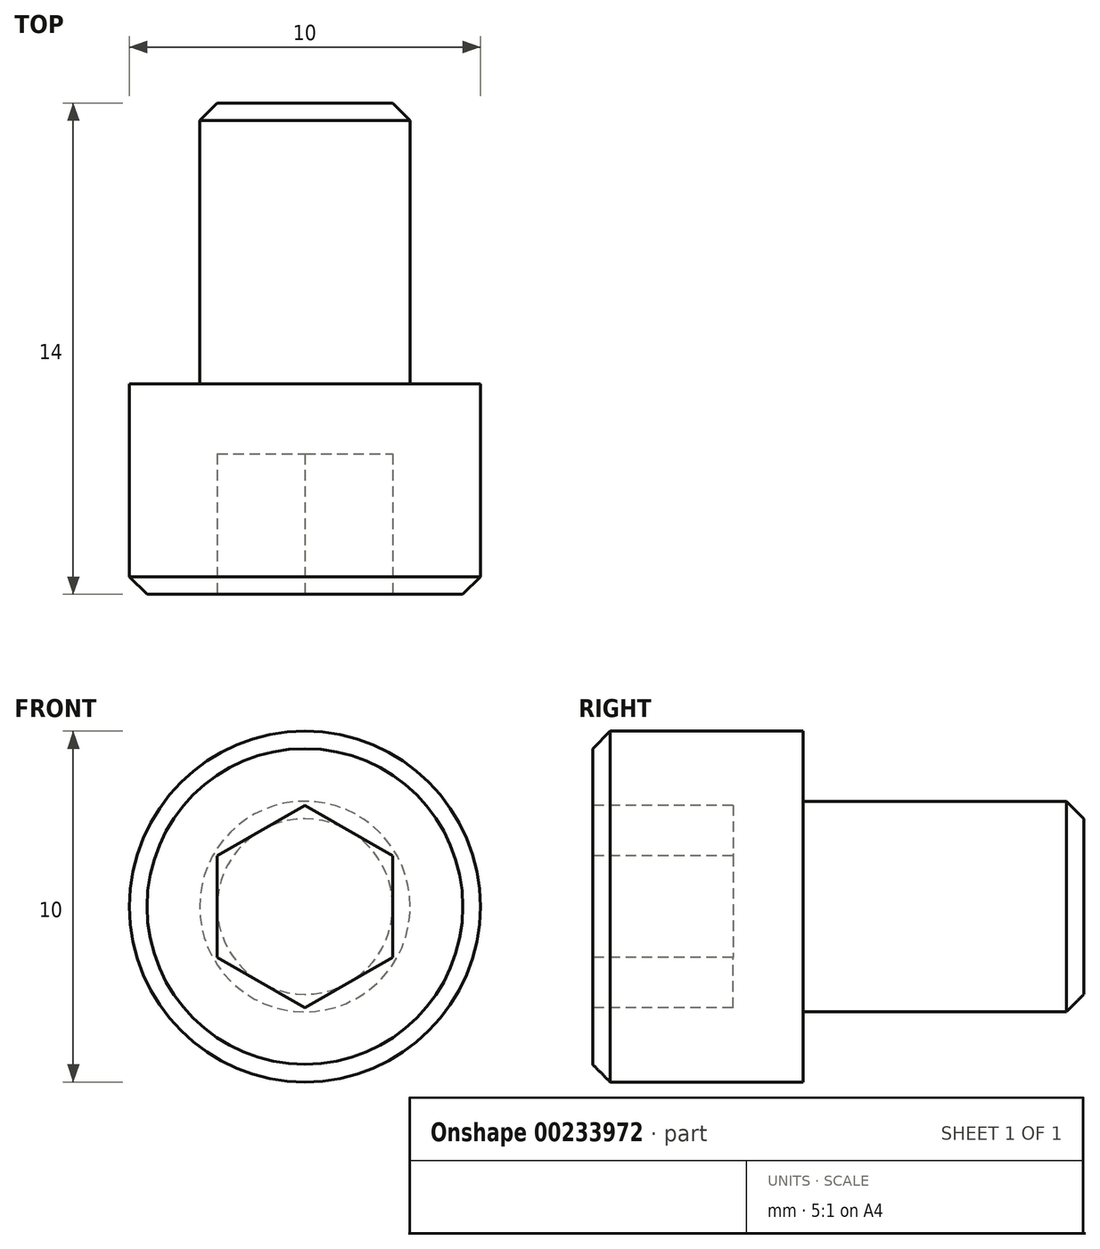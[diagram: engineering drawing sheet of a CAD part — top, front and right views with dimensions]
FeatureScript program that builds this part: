
annotation { "Feature Type Name" : "Feature", "Feature Type Description" : "" }
export const myFeature = defineFeature(function(context is Context, id is Id, definition is map)
    precondition{}
    {
        {
            var Q0;
            Q0=qCreatedBy(makeId("Front.planeOp"),FACE);
            var sketch = newSketch(context, id + "F0", { "sketchPlane" : qUnion([Q0])});
            skCircle(sketch, "E0", {"center": v(0, 0) * mm, "radius": 5 * mm});
            skCircle(sketch, "E1", {"center": v(0, 0) * mm, "radius": 3 * mm});
            skSolve(sketch);
        }
        {
            var Q0;
            Q0=makeQuery(id+"F0.imprint","IMPRINT",FACE,{"disambiguationData":[TD([[makeQuery(id+"F0.imprint","IMPRINT",EDGE,{"derivedFrom":sQuery(id+"F0.wireOp",EDGE,"E0")}),1.0]])]});
            var Q1;
            Q1=makeQuery(id+"F0.imprint","IMPRINT",FACE,{"disambiguationData":[TD([[makeQuery(id+"F0.imprint","IMPRINT",EDGE,{"derivedFrom":sQuery(id+"F0.wireOp",EDGE,"E1")}),1.0]])]});
            extrude(context, id + "F1", {"entities" : qUnion([Q0, Q1]), "depth" : 6 * mm, "offsetDistance" : 25 * mm});
        }
        {
            var Q0;
            Q0=makeQuery(id+"F0.imprint","IMPRINT",FACE,{"disambiguationData":[TD([[makeQuery(id+"F0.imprint","IMPRINT",EDGE,{"derivedFrom":sQuery(id+"F0.wireOp",EDGE,"E1")}),1.0]])]});
            extrude(context, id + "F2", {"entities" : qUnion([Q0]), "operationType" : NewBodyOperationType.ADD, "oppositeDirection" : true, "depth" : 8 * mm, "offsetDistance" : 25 * mm});
        }
        {
            var Q0;
            Q0=makeQuery(id+"F1.opExtrude","CAP_EDGE",EDGE,{"disambiguationData":[OSD([sQuery(id+"F0.wireOp",EDGE,"E0")])],"isStart":false});
            var Q1;
            Q1=makeQuery(id+"F2.opExtrude","CAP_EDGE",EDGE,{"disambiguationData":[OSD([sQuery(id+"F0.wireOp",EDGE,"E1")])],"isStart":false});
            chamfer(context, id + "F3", {"entities" : qUnion([Q0, Q1]), "width" : 0.5 * mm, "tangentPropagation" : true});
        }
        {
            var Q0;
            Q0=makeQuery(id+"F1.opExtrude","CAP_FACE",FACE,{"disambiguationData":[OSD([sQuery(id+"F0.wireOp",EDGE,"E0")])],"isStart":false});
            var sketch = newSketch(context, id + "F4", { "sketchPlane" : qUnion([Q0])});
            skCircle(sketch, "E2.cCircle", {"center": v(0, 0) * mm, "radius": 2.5 * mm, "construction": true});
            skLineSegment(sketch, "E2.0", {"start": v(2.5, 1.44) * mm, "end": v(2.5, -1.44) * mm});
            skLineSegment(sketch, "E2.1", {"start": v(2.5, -1.44) * mm, "end": v(0, -2.89) * mm});
            skLineSegment(sketch, "E2.2", {"start": v(0, -2.89) * mm, "end": v(-2.5, -1.44) * mm});
            skLineSegment(sketch, "E2.3", {"start": v(-2.5, -1.44) * mm, "end": v(-2.5, 1.44) * mm});
            skLineSegment(sketch, "E2.4", {"start": v(-2.5, 1.44) * mm, "end": v(0, 2.89) * mm});
            skLineSegment(sketch, "E2.5", {"start": v(0, 2.89) * mm, "end": v(2.5, 1.44) * mm});
            skPoint(sketch, "E2.0.midPoint", {"position": v(2.5, 0) * mm});
            skSolve(sketch);
        }
        {
            var Q0;
            Q0=makeQuery(id+"F4.imprint","IMPRINT",FACE,{"disambiguationData":[TD([[makeQuery(id+"F4.imprint","IMPRINT",EDGE,{"derivedFrom":sQuery(id+"F4.wireOp",EDGE,"E2.0")}),-1.0]])]});
            extrude(context, id + "F5", {"entities" : qUnion([Q0]), "operationType" : NewBodyOperationType.REMOVE, "oppositeDirection" : true, "depth" : 4 * mm, "offsetDistance" : 25 * mm});
        }
    });
